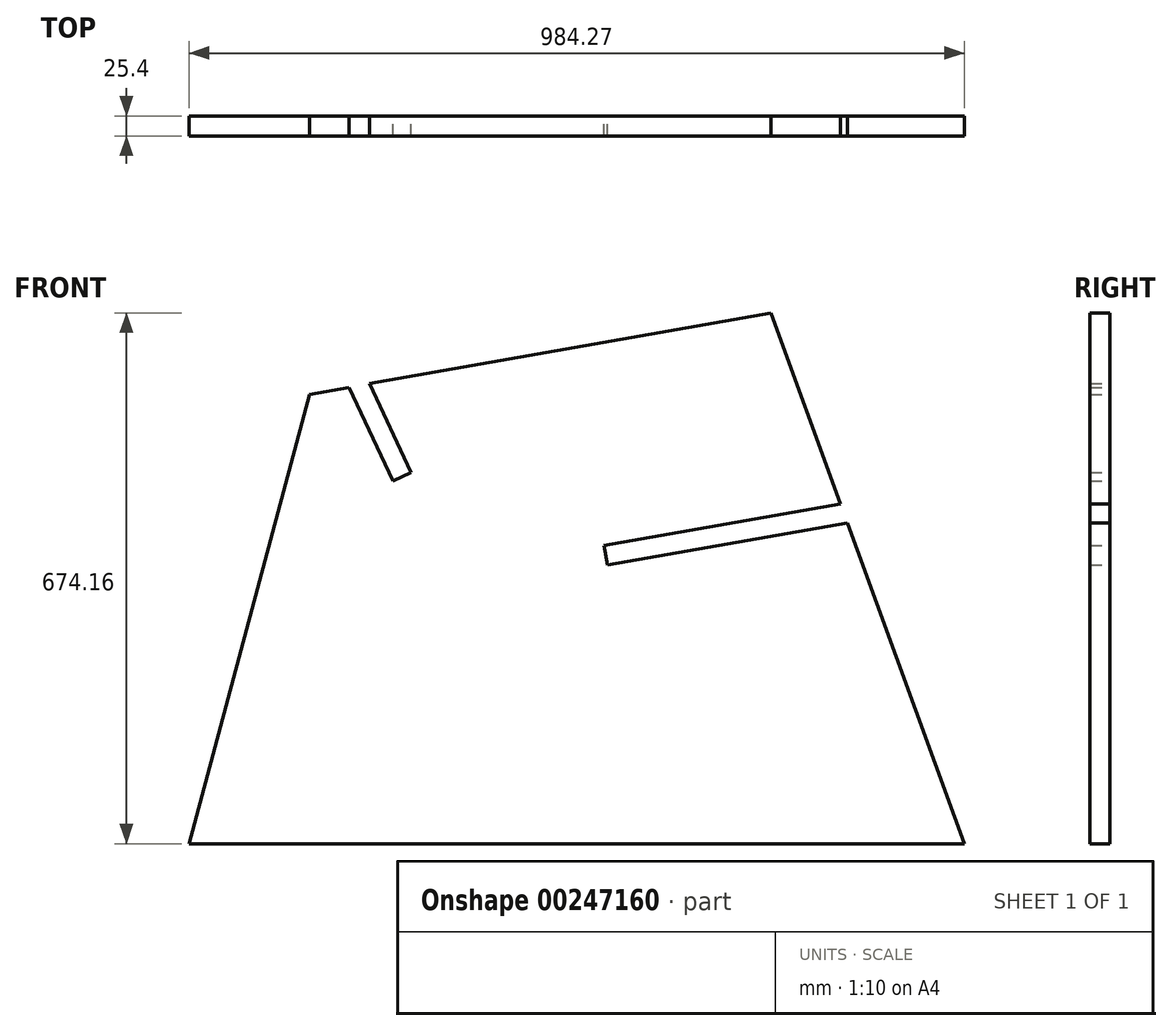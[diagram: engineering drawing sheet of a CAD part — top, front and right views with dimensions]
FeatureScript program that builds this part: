
annotation { "Feature Type Name" : "Feature", "Feature Type Description" : "" }
export const myFeature = defineFeature(function(context is Context, id is Id, definition is map)
    precondition{}
    {
        {
            var Q0;
            Q0=qCreatedBy(makeId("Front.planeOp"),FACE);
            var sketch = newSketch(context, id + "F0", { "sketchPlane" : qUnion([Q0])});
            skLineSegment(sketch, "E0", {"start": v(-701.58, -58.15) * mm, "end": v(282.7, -58.15) * mm});
            skLineSegment(sketch, "E1", {"start": v(282.7, -58.15) * mm, "end": v(134.35, 349.41) * mm});
            skLineSegment(sketch, "E2", {"start": v(37.31, 616.01) * mm, "end": v(-472.7, 526.09) * mm});
            skLineSegment(sketch, "E3", {"start": v(125.53, 373.65) * mm, "end": v(-174.64, 320.72) * mm});
            skLineSegment(sketch, "E4", {"start": v(-174.64, 320.72) * mm, "end": v(-170.23, 295.7) * mm});
            skLineSegment(sketch, "E5", {"start": v(-170.23, 295.7) * mm, "end": v(134.35, 349.41) * mm});
            skLineSegment(sketch, "E6.trimOffspring", {"start": v(125.53, 373.65) * mm, "end": v(37.31, 616.01) * mm});
            skPoint(sketch, "E7.visualSharp", {"position": v(37.31, 616.01) * mm});
            skPoint(sketch, "E8.visualSharp", {"position": v(282.7, -58.15) * mm});
            skLineSegment(sketch, "E9", {"start": v(-420, 413.1) * mm, "end": v(-472.7, 526.09) * mm});
            skLineSegment(sketch, "E10", {"start": v(-420, 413.1) * mm, "end": v(-443.02, 402.36) * mm});
            skLineSegment(sketch, "E11", {"start": v(-443.02, 402.36) * mm, "end": v(-498.59, 521.52) * mm});
            skLineSegment(sketch, "E12", {"start": v(-701.58, -58.15) * mm, "end": v(-548.62, 512.7) * mm});
            skLineSegment(sketch, "E13", {"start": v(-498.59, 521.52) * mm, "end": v(-548.62, 512.7) * mm});
            skLineSegment(sketch, "E14", {"start": v(-266.38, 305) * mm, "end": v(-353.32, 281.93) * mm});
            skLineSegment(sketch, "E15", {"start": v(-353.32, 281.93) * mm, "end": v(-379.94, 336.93) * mm});
            skSolve(sketch);
        }
        {
            var Q0;
            Q0=makeQuery(id+"F0.imprint","IMPRINT",FACE,{"disambiguationData":[TD([[makeQuery(id+"F0.imprint","IMPRINT",EDGE,{"derivedFrom":sQuery(id+"F0.wireOp",EDGE,"E0")}),1.0]])]});
            extrude(context, id + "F1", {"entities" : qUnion([Q0]), "depth" : 25.4 * mm});
        }
    });
